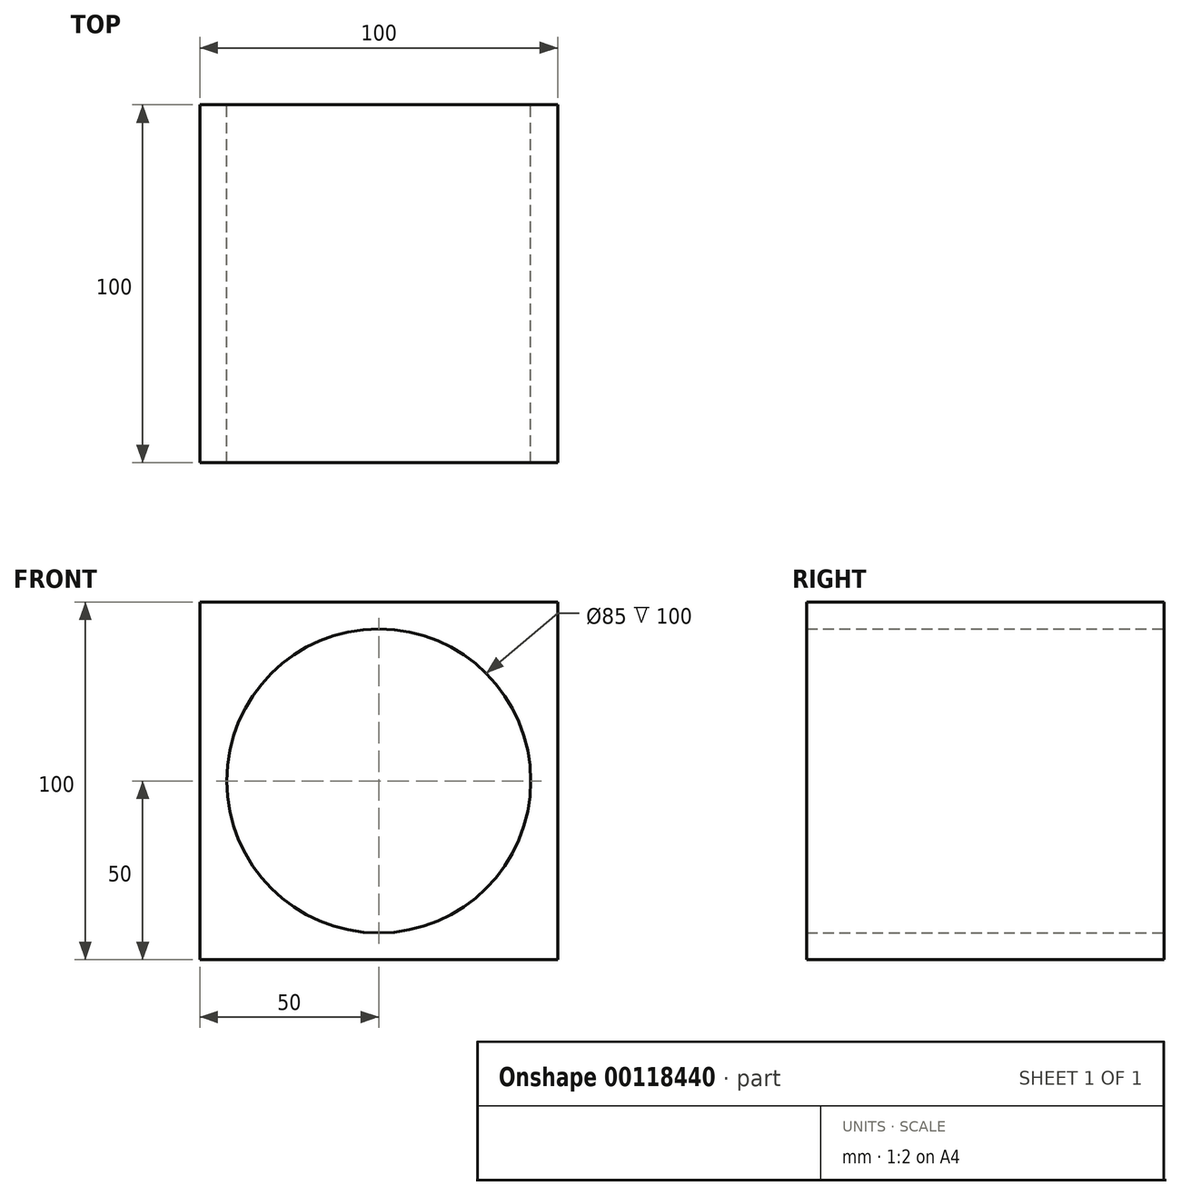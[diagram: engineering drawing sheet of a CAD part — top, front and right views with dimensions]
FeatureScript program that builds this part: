
annotation { "Feature Type Name" : "Feature", "Feature Type Description" : "" }
export const myFeature = defineFeature(function(context is Context, id is Id, definition is map)
    precondition{}
    {
        {
            var Q0;
            Q0=qCreatedBy(makeId("Front.planeOp"),FACE);
            var sketch = newSketch(context, id + "F0", { "sketchPlane" : qUnion([Q0])});
            skLineSegment(sketch, "E0.bottom", {"start": v(-50, -50) * mm, "end": v(50, -50) * mm});
            skLineSegment(sketch, "E0.top", {"start": v(-50, 50) * mm, "end": v(50, 50) * mm});
            skLineSegment(sketch, "E0.left", {"start": v(-50, -50) * mm, "end": v(-50, 50) * mm});
            skLineSegment(sketch, "E0.right", {"start": v(50, -50) * mm, "end": v(50, 50) * mm});
            skPoint(sketch, "E0.middle", {"position": v(0, 0) * mm});
            skCircle(sketch, "E1", {"center": v(0, 0) * mm, "radius": 42.5 * mm});
            skSolve(sketch);
        }
        {
            var Q0;
            Q0 = qSketchRegion(id + "F0", true);
            extrude(context, id + "F1", {"entities" : qUnion([Q0]), "endBound" : BoundingType.SYMMETRIC, "depth" : 100 * mm});
        }
    });
